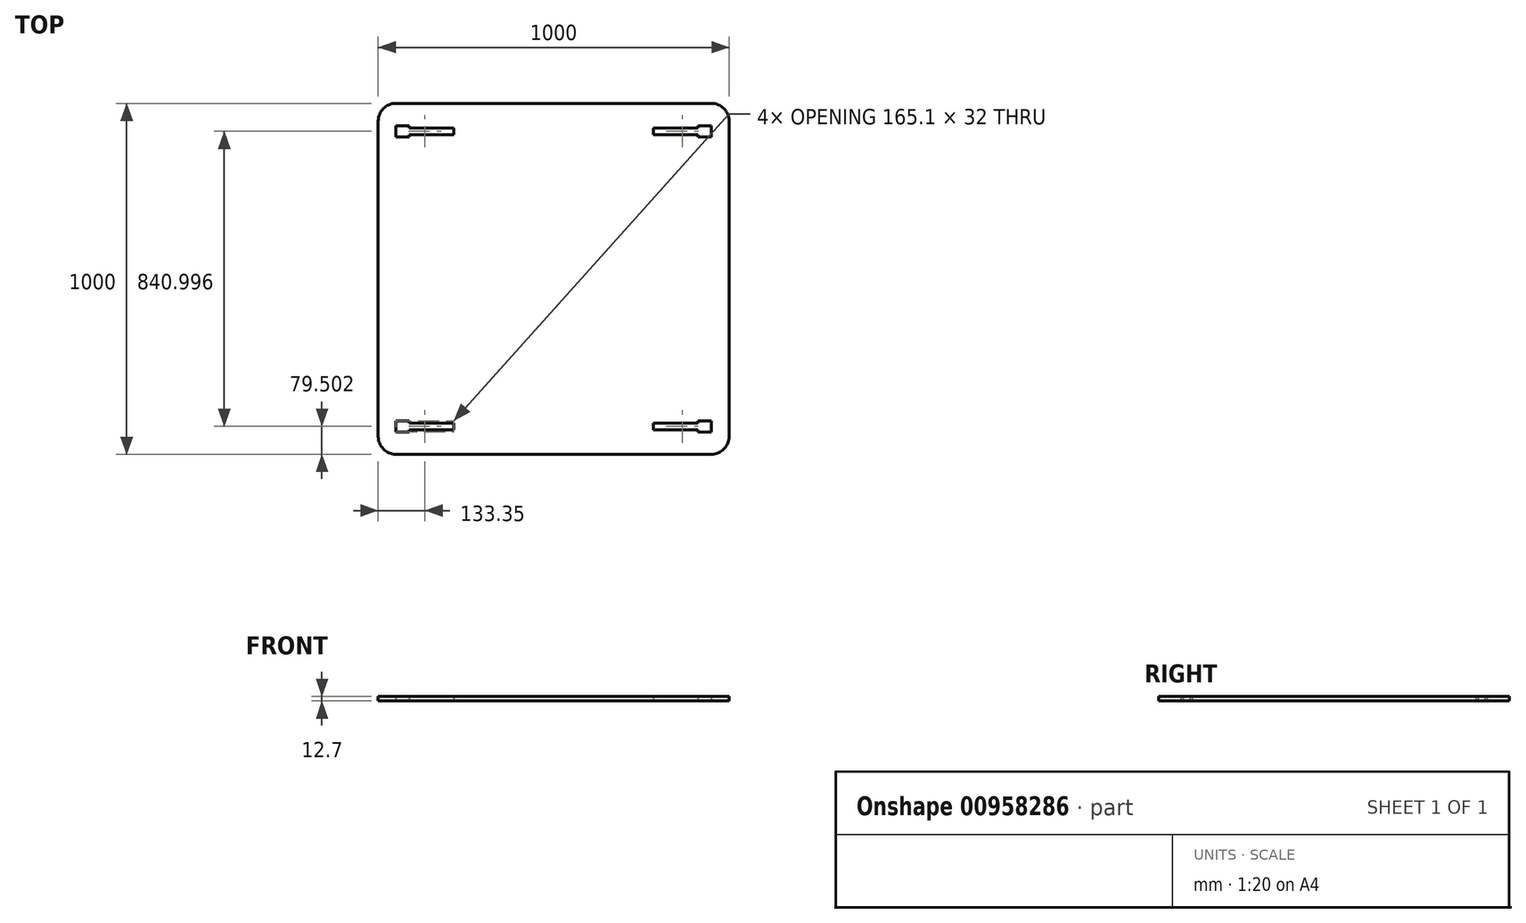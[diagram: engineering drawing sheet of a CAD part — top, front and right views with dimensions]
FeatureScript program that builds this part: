
annotation { "Feature Type Name" : "Feature", "Feature Type Description" : "" }
export const myFeature = defineFeature(function(context is Context, id is Id, definition is map)
    precondition{}
    {
        {
            var Q0;
            Q0=qCreatedBy(makeId("Top.planeOp"),FACE);
            var sketch = newSketch(context, id + "F0", { "sketchPlane" : qUnion([Q0])});
            skLineSegment(sketch, "E0.bottom", {"start": v(-449.2, 500) * mm, "end": v(449.2, 500) * mm});
            skLineSegment(sketch, "E0.top", {"start": v(-449.2, -500) * mm, "end": v(449.2, -500) * mm});
            skLineSegment(sketch, "E0.left", {"start": v(-500, 449.2) * mm, "end": v(-500, -449.2) * mm});
            skLineSegment(sketch, "E0.right", {"start": v(500, 449.2) * mm, "end": v(500, -449.2) * mm});
            skPoint(sketch, "E0.middle", {"position": v(0, 0) * mm});
            skLineSegment(sketch, "E1.bottom", {"start": v(-449.2, -404.5) * mm, "end": v(-411.1, -404.5) * mm});
            skLineSegment(sketch, "E1.top", {"start": v(-449.2, -436.5) * mm, "end": v(-411.1, -436.5) * mm});
            skLineSegment(sketch, "E1.left", {"start": v(-449.2, -404.5) * mm, "end": v(-449.2, -436.5) * mm});
            skLineSegment(sketch, "E2.bottom", {"start": v(-411.1, -410.97) * mm, "end": v(-284.1, -410.97) * mm});
            skLineSegment(sketch, "E2.top", {"start": v(-411.1, -430.02) * mm, "end": v(-284.1, -430.02) * mm});
            skLineSegment(sketch, "E2.right", {"start": v(-284.1, -410.97) * mm, "end": v(-284.1, -430.02) * mm});
            skLineSegment(sketch, "E3", {"start": v(-411.1, -404.5) * mm, "end": v(-411.1, -410.97) * mm});
            skLineSegment(sketch, "E4", {"start": v(-411.1, -436.5) * mm, "end": v(-411.1, -430.02) * mm});
            skLineSegment(sketch, "E5", {"start": v(0, -500) * mm, "end": v(0, 500) * mm});
            skLineSegment(sketch, "E6.MirrorCS", {"start": v(284.1, -410.97) * mm, "end": v(284.1, -430.02) * mm});
            skLineSegment(sketch, "E7.MirrorCS", {"start": v(411.1, -410.97) * mm, "end": v(284.1, -410.97) * mm});
            skLineSegment(sketch, "E8.MirrorCS", {"start": v(411.1, -430.02) * mm, "end": v(284.1, -430.02) * mm});
            skLineSegment(sketch, "E9.MirrorCS", {"start": v(449.2, -436.5) * mm, "end": v(411.1, -436.5) * mm});
            skLineSegment(sketch, "E10.MirrorCS", {"start": v(449.2, -404.5) * mm, "end": v(411.1, -404.5) * mm});
            skLineSegment(sketch, "E11.MirrorCS", {"start": v(449.2, -404.5) * mm, "end": v(449.2, -436.5) * mm});
            skLineSegment(sketch, "E12.MirrorCS", {"start": v(411.1, -404.5) * mm, "end": v(411.1, -410.97) * mm});
            skLineSegment(sketch, "E13.MirrorCS", {"start": v(411.1, -436.5) * mm, "end": v(411.1, -430.02) * mm});
            skLineSegment(sketch, "E14", {"start": v(-500, 0) * mm, "end": v(500, 0) * mm});
            skLineSegment(sketch, "E15.MirrorCS", {"start": v(411.1, 436.5) * mm, "end": v(411.1, 430.02) * mm});
            skLineSegment(sketch, "E16.MirrorCS", {"start": v(449.2, 404.5) * mm, "end": v(411.1, 404.5) * mm});
            skLineSegment(sketch, "E17.MirrorCS", {"start": v(449.2, 436.5) * mm, "end": v(411.1, 436.5) * mm});
            skLineSegment(sketch, "E18.MirrorCS", {"start": v(284.1, 410.97) * mm, "end": v(284.1, 430.02) * mm});
            skLineSegment(sketch, "E19.MirrorCS", {"start": v(449.2, 404.5) * mm, "end": v(449.2, 436.5) * mm});
            skLineSegment(sketch, "E20.MirrorCS", {"start": v(411.1, 404.5) * mm, "end": v(411.1, 410.97) * mm});
            skLineSegment(sketch, "E21.MirrorCS", {"start": v(411.1, 430.02) * mm, "end": v(284.1, 430.02) * mm});
            skLineSegment(sketch, "E22.MirrorCS", {"start": v(411.1, 410.97) * mm, "end": v(284.1, 410.97) * mm});
            skLineSegment(sketch, "E23.MirrorCS", {"start": v(-411.1, 404.5) * mm, "end": v(-411.1, 410.97) * mm});
            skLineSegment(sketch, "E24.MirrorCS", {"start": v(-411.1, 436.5) * mm, "end": v(-411.1, 430.02) * mm});
            skLineSegment(sketch, "E25.MirrorCS", {"start": v(-284.1, 410.97) * mm, "end": v(-284.1, 430.02) * mm});
            skLineSegment(sketch, "E26.MirrorCS", {"start": v(-449.2, 436.5) * mm, "end": v(-411.1, 436.5) * mm});
            skLineSegment(sketch, "E27.MirrorCS", {"start": v(-449.2, 404.5) * mm, "end": v(-449.2, 436.5) * mm});
            skLineSegment(sketch, "E28.MirrorCS", {"start": v(-449.2, 404.5) * mm, "end": v(-411.1, 404.5) * mm});
            skLineSegment(sketch, "E29.MirrorCS", {"start": v(-411.1, 410.97) * mm, "end": v(-284.1, 410.97) * mm});
            skLineSegment(sketch, "E30.MirrorCS", {"start": v(-411.1, 430.02) * mm, "end": v(-284.1, 430.02) * mm});
            skPoint(sketch, "E31.visualSharp", {"position": v(-500, 500) * mm});
            skArc(sketch, "E31.filletArc", {"start": v(-449.2, 500) * mm, "mid": v(-485.12, 485.12) * mm, "end": v(-500, 449.2) * mm});
            skPoint(sketch, "E32.visualSharp", {"position": v(500, 500) * mm});
            skArc(sketch, "E32.filletArc", {"start": v(500, 449.2) * mm, "mid": v(485.12, 485.12) * mm, "end": v(449.2, 500) * mm});
            skPoint(sketch, "E33.visualSharp", {"position": v(500, -500) * mm});
            skArc(sketch, "E33.filletArc", {"start": v(449.2, -500) * mm, "mid": v(485.12, -485.12) * mm, "end": v(500, -449.2) * mm});
            skPoint(sketch, "E34.visualSharp", {"position": v(-500, -500) * mm});
            skArc(sketch, "E34.filletArc", {"start": v(-500, -449.2) * mm, "mid": v(-485.12, -485.12) * mm, "end": v(-449.2, -500) * mm});
            skSolve(sketch);
        }
        {
            var Q0;
            Q0=makeQuery(id+"F0.imprint","IMPRINT",FACE,{"disambiguationData":[TD([[makeQuery(id+"F0.imprint","IMPRINT",EDGE,{"derivedFrom":sQuery(id+"F0.wireOp",EDGE,"E23.MirrorCS")}),-1.0]])]});
            var Q1;
            Q1=makeQuery(id+"F0.imprint","IMPRINT",FACE,{"disambiguationData":[TD([[makeQuery(id+"F0.imprint","IMPRINT",EDGE,{"derivedFrom":sQuery(id+"F0.wireOp",EDGE,"E15.MirrorCS")}),-1.0]])]});
            var Q2;
            Q2=makeQuery(id+"F0.imprint","IMPRINT",FACE,{"disambiguationData":[TD([[makeQuery(id+"F0.imprint","IMPRINT",EDGE,{"derivedFrom":sQuery(id+"F0.wireOp",EDGE,"E6.MirrorCS")}),-1.0]])]});
            var Q3;
            Q3=makeQuery(id+"F0.imprint","IMPRINT",FACE,{"disambiguationData":[TD([[makeQuery(id+"F0.imprint","IMPRINT",EDGE,{"derivedFrom":sQuery(id+"F0.wireOp",EDGE,"E1.bottom")}),1.0]])]});
            extrude(context, id + "F1", {"entities" : qUnion([Q0, Q1, Q2, Q3]), "depth" : 12.7 * mm, "offsetDistance" : 25.4 * mm});
        }
    });
